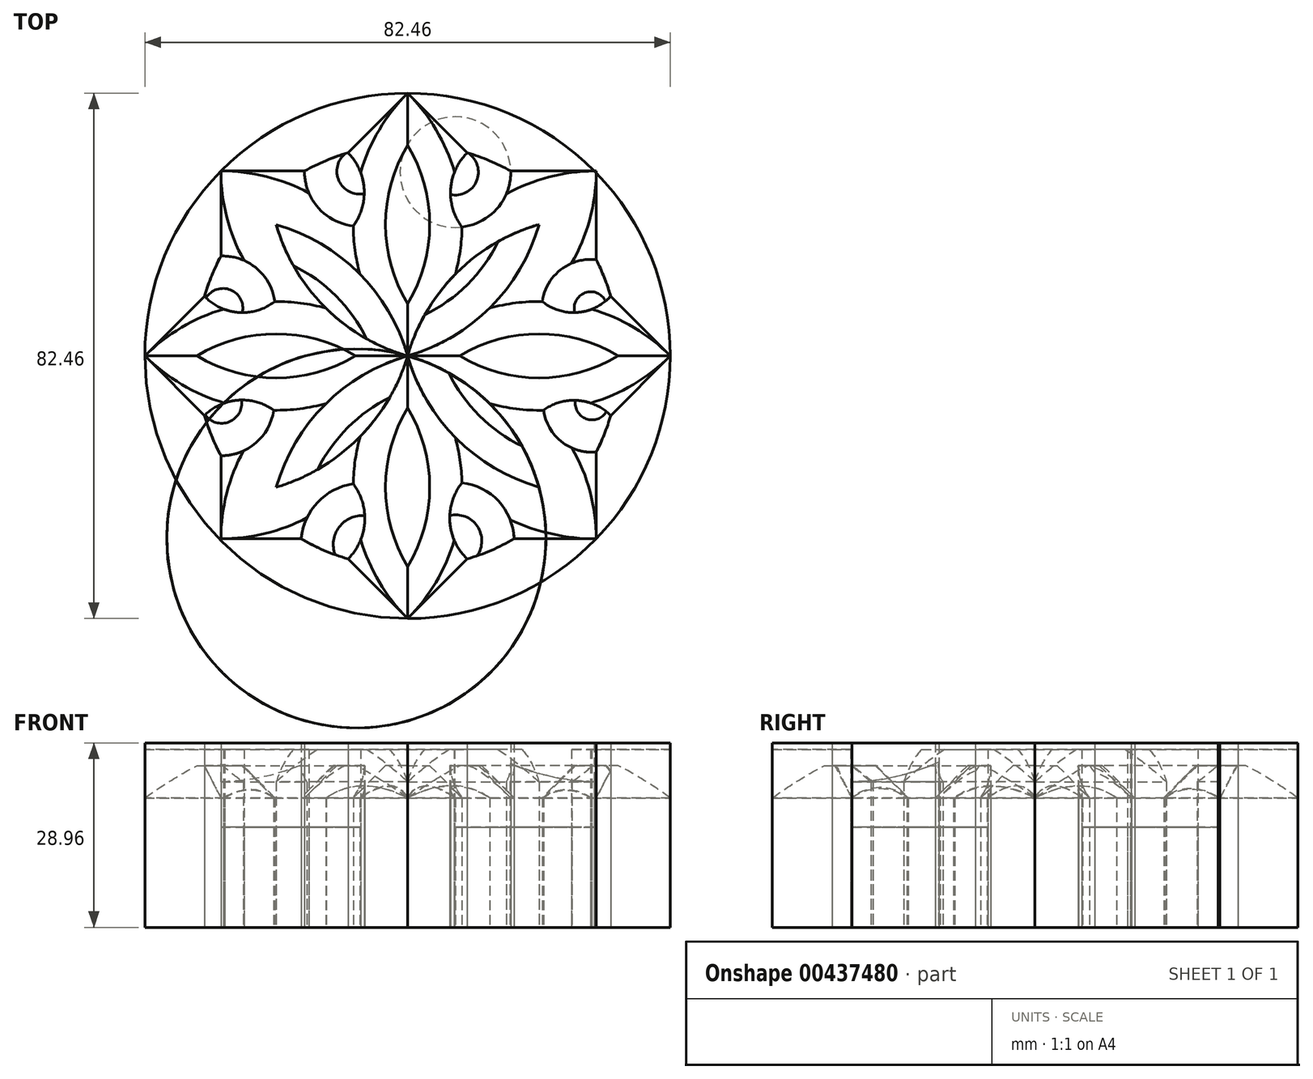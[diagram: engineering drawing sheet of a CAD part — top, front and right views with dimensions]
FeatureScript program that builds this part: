
annotation { "Feature Type Name" : "Feature", "Feature Type Description" : "" }
export const myFeature = defineFeature(function(context is Context, id is Id, definition is map)
    precondition{}
    {
        {
            var Q0;
            Q0=qCreatedBy(makeId("Top.planeOp"),FACE);
            var sketch = newSketch(context, id + "F0", { "sketchPlane" : qUnion([Q0])});
            skCircle(sketch, "E0", {"center": v(0, 0) * mm, "radius": 41.23 * mm});
            skArc(sketch, "E1", {"start": v(-9.36, 31.87) * mm, "mid": v(-12.85, 30.63) * mm, "end": v(-16.18, 29.01) * mm});
            skLineSegment(sketch, "E2", {"start": v(41.23, 0) * mm, "end": v(31.87, 9.36) * mm});
            skLineSegment(sketch, "E3", {"start": v(0, 41.23) * mm, "end": v(-9.36, 31.87) * mm});
            skLineSegment(sketch, "E4", {"start": v(-41.23, 0) * mm, "end": v(-31.87, -9.36) * mm});
            skLineSegment(sketch, "E5", {"start": v(0, -41.23) * mm, "end": v(9.36, -31.87) * mm});
            skLineSegment(sketch, "E6.bottom", {"start": v(-29.3, 29.01) * mm, "end": v(-16.18, 29.01) * mm});
            skLineSegment(sketch, "E6.top", {"start": v(-29.3, -28.71) * mm, "end": v(-16.71, -28.71) * mm});
            skLineSegment(sketch, "E6.left", {"start": v(-29.3, 29.01) * mm, "end": v(-29.3, 15.66) * mm});
            skLineSegment(sketch, "E6.right", {"start": v(29.6, 29.01) * mm, "end": v(29.6, 15.1) * mm});
            skLineSegment(sketch, "E7.trimOffspring", {"start": v(-31.87, 9.36) * mm, "end": v(-41.23, 0) * mm});
            skLineSegment(sketch, "E8.trimOffspring", {"start": v(-9.36, -31.87) * mm, "end": v(0, -41.23) * mm});
            skLineSegment(sketch, "E9.trimOffspring", {"start": v(31.87, -9.36) * mm, "end": v(41.23, 0) * mm});
            skLineSegment(sketch, "E10.trimOffspring", {"start": v(9.36, 31.87) * mm, "end": v(0, 41.23) * mm});
            skLineSegment(sketch, "E11.trimOffspring", {"start": v(16.18, 29.01) * mm, "end": v(29.6, 29.01) * mm});
            skLineSegment(sketch, "E12.trimOffspring", {"start": v(29.6, -15.1) * mm, "end": v(29.6, -28.71) * mm});
            skLineSegment(sketch, "E13.trimOffspring", {"start": v(-29.3, -15.66) * mm, "end": v(-29.3, -28.71) * mm});
            skLineSegment(sketch, "E14.trimOffspring", {"start": v(16.71, -28.71) * mm, "end": v(29.6, -28.71) * mm});
            skArc(sketch, "E15.trimOffspring", {"start": v(-29.3, 15.66) * mm, "mid": v(-30.75, 12.57) * mm, "end": v(-31.87, 9.36) * mm});
            skArc(sketch, "E16.trimOffspring", {"start": v(-31.87, -9.36) * mm, "mid": v(-30.75, -12.57) * mm, "end": v(-29.3, -15.66) * mm});
            skArc(sketch, "E17.trimOffspring", {"start": v(-16.71, -28.71) * mm, "mid": v(-13.13, -30.51) * mm, "end": v(-9.36, -31.87) * mm});
            skArc(sketch, "E18.trimOffspring", {"start": v(9.36, -31.87) * mm, "mid": v(13.13, -30.51) * mm, "end": v(16.71, -28.71) * mm});
            skArc(sketch, "E19.trimOffspring", {"start": v(29.6, -15.1) * mm, "mid": v(30.87, -12.28) * mm, "end": v(31.87, -9.36) * mm});
            skArc(sketch, "E20.trimOffspring", {"start": v(31.87, 9.36) * mm, "mid": v(30.87, 12.28) * mm, "end": v(29.6, 15.1) * mm});
            skArc(sketch, "E21.trimOffspring", {"start": v(16.18, 29.01) * mm, "mid": v(12.85, 30.63) * mm, "end": v(9.36, 31.87) * mm});
            skArc(sketch, "E22", {"start": v(7.47, 12.8) * mm, "mid": v(8.24, 16.47) * mm, "end": v(8.54, 20.21) * mm});
            skArc(sketch, "E23", {"start": v(0, 41.23) * mm, "mid": v(-4.47, 35.47) * mm, "end": v(-7.37, 28.78) * mm});
            skArc(sketch, "E24", {"start": v(29.6, 29.01) * mm, "mid": v(22.32, 28.1) * mm, "end": v(15.5, 25.44) * mm});
            skArc(sketch, "E25", {"start": v(41.23, 0) * mm, "mid": v(35.53, 4.43) * mm, "end": v(28.92, 7.33) * mm});
            skArc(sketch, "E26", {"start": v(12.9, -7.5) * mm, "mid": v(17.06, -8.32) * mm, "end": v(21.3, -8.53) * mm});
            skArc(sketch, "E27", {"start": v(29.6, -28.71) * mm, "mid": v(28.63, -21.34) * mm, "end": v(25.8, -14.46) * mm});
            skArc(sketch, "E28", {"start": v(0, -41.23) * mm, "mid": v(4.43, -35.54) * mm, "end": v(7.32, -28.94) * mm});
            skArc(sketch, "E29", {"start": v(-7.43, -12.63) * mm, "mid": v(-8.22, -16.32) * mm, "end": v(-8.53, -20.08) * mm});
            skArc(sketch, "E30", {"start": v(-29.3, -28.71) * mm, "mid": v(-22.35, -27.87) * mm, "end": v(-15.79, -25.41) * mm});
            skArc(sketch, "E31", {"start": v(-41.23, 0) * mm, "mid": v(-35.44, -4.49) * mm, "end": v(-28.72, -7.4) * mm});
            skArc(sketch, "E32", {"start": v(-12.82, 7.48) * mm, "mid": v(-16.8, 8.29) * mm, "end": v(-20.84, 8.54) * mm});
            skArc(sketch, "E33", {"start": v(-15.48, 25.55) * mm, "mid": v(-22.17, 28.13) * mm, "end": v(-29.3, 29.01) * mm});
            skArc(sketch, "E34", {"start": v(-29.3, 29.01) * mm, "mid": v(-28.38, 21.76) * mm, "end": v(-25.68, 14.98) * mm});
            skArc(sketch, "E35.trimOffspring", {"start": v(-25.77, -14.91) * mm, "mid": v(-28.4, -21.59) * mm, "end": v(-29.3, -28.71) * mm});
            skArc(sketch, "E36.trimOffspring", {"start": v(25.72, 14.52) * mm, "mid": v(28.6, 21.51) * mm, "end": v(29.6, 29.01) * mm});
            skArc(sketch, "E37", {"start": v(-8.54, 20.39) * mm, "mid": v(-6.83, 26.28) * mm, "end": v(-9.36, 31.87) * mm});
            skArc(sketch, "E38", {"start": v(-16.18, 29.01) * mm, "mid": v(-14.01, 23.24) * mm, "end": v(-8.54, 20.39) * mm});
            skArc(sketch, "E39", {"start": v(9.36, 31.87) * mm, "mid": v(6.76, 26.2) * mm, "end": v(8.54, 20.21) * mm});
            skArc(sketch, "E40", {"start": v(8.54, 20.21) * mm, "mid": v(14.06, 23.14) * mm, "end": v(16.18, 29.01) * mm});
            skArc(sketch, "E41", {"start": v(29.6, 15.1) * mm, "mid": v(24.03, 13.53) * mm, "end": v(21.13, 8.53) * mm});
            skArc(sketch, "E42", {"start": v(21.13, 8.53) * mm, "mid": v(26.67, 6.82) * mm, "end": v(31.87, 9.36) * mm});
            skArc(sketch, "E43", {"start": v(-20.84, 8.54) * mm, "mid": v(-23.69, 13.74) * mm, "end": v(-29.3, 15.66) * mm});
            skArc(sketch, "E44", {"start": v(-31.87, 9.36) * mm, "mid": v(-26.52, 6.81) * mm, "end": v(-20.84, 8.54) * mm});
            skArc(sketch, "E45", {"start": v(-21.02, -8.54) * mm, "mid": v(-26.6, -6.95) * mm, "end": v(-31.87, -9.36) * mm});
            skArc(sketch, "E46", {"start": v(-29.3, -15.66) * mm, "mid": v(-23.81, -13.66) * mm, "end": v(-21.02, -8.54) * mm});
            skArc(sketch, "E47", {"start": v(-8.53, -20.08) * mm, "mid": v(-14.11, -22.99) * mm, "end": v(-16.71, -28.71) * mm});
            skArc(sketch, "E48", {"start": v(-9.36, -31.87) * mm, "mid": v(-6.74, -26.13) * mm, "end": v(-8.53, -20.08) * mm});
            skArc(sketch, "E49", {"start": v(8.53, -19.91) * mm, "mid": v(6.63, -26.05) * mm, "end": v(9.36, -31.87) * mm});
            skArc(sketch, "E50", {"start": v(16.71, -28.71) * mm, "mid": v(14.26, -22.79) * mm, "end": v(8.53, -19.91) * mm});
            skArc(sketch, "E51", {"start": v(31.87, -9.36) * mm, "mid": v(26.74, -7) * mm, "end": v(21.3, -8.53) * mm});
            skArc(sketch, "E52", {"start": v(21.3, -8.53) * mm, "mid": v(24.15, -13.46) * mm, "end": v(29.6, -15.1) * mm});
            skArc(sketch, "E53.trimOffspring", {"start": v(-8.54, 20.39) * mm, "mid": v(-8.26, 16.57) * mm, "end": v(-7.48, 12.82) * mm});
            skArc(sketch, "E54.trimOffspring", {"start": v(-28.87, 7.35) * mm, "mid": v(-35.51, 4.45) * mm, "end": v(-41.23, 0) * mm});
            skArc(sketch, "E55.trimOffspring", {"start": v(-21.02, -8.54) * mm, "mid": v(-16.86, -8.3) * mm, "end": v(-12.79, -7.47) * mm});
            skArc(sketch, "E56.trimOffspring", {"start": v(-7.36, -28.83) * mm, "mid": v(-4.46, -35.5) * mm, "end": v(0, -41.23) * mm});
            skArc(sketch, "E57.trimOffspring", {"start": v(8.53, -19.91) * mm, "mid": v(8.22, -16.3) * mm, "end": v(7.46, -12.77) * mm});
            skArc(sketch, "E58.trimOffspring", {"start": v(28.7, -7.4) * mm, "mid": v(35.44, -4.5) * mm, "end": v(41.23, 0) * mm});
            skArc(sketch, "E59.trimOffspring", {"start": v(7.36, 28.84) * mm, "mid": v(4.46, 35.5) * mm, "end": v(0, 41.23) * mm});
            skArc(sketch, "E60.trimOffspring", {"start": v(21.13, 8.53) * mm, "mid": v(16.96, 8.3) * mm, "end": v(12.86, 7.49) * mm});
            skArc(sketch, "E61", {"start": v(0, 0) * mm, "mid": v(-7.64, 12.98) * mm, "end": v(-20.62, 20.62) * mm});
            skArc(sketch, "E62", {"start": v(-20.62, 20.62) * mm, "mid": v(-12.98, 7.63) * mm, "end": v(0, 0) * mm});
            skArc(sketch, "E63", {"start": v(20.62, 20.62) * mm, "mid": v(7.64, 12.97) * mm, "end": v(0, 0) * mm});
            skArc(sketch, "E64", {"start": v(0, 0) * mm, "mid": v(13, 7.62) * mm, "end": v(20.62, 20.62) * mm});
            skArc(sketch, "E65", {"start": v(20.62, -20.62) * mm, "mid": v(13, -7.61) * mm, "end": v(0, 0) * mm});
            skArc(sketch, "E66", {"start": v(0, 0) * mm, "mid": v(7.65, -12.96) * mm, "end": v(20.62, -20.62) * mm});
            skArc(sketch, "E67", {"start": v(-20.62, -20.62) * mm, "mid": v(-7.7, -12.91) * mm, "end": v(0, 0) * mm});
            skArc(sketch, "E68", {"start": v(0, 0) * mm, "mid": v(-12.97, -7.65) * mm, "end": v(-20.62, -20.62) * mm});
            skArc(sketch, "E69", {"start": v(16.1, -25.72) * mm, "mid": v(22.68, -27.95) * mm, "end": v(29.6, -28.71) * mm});
            skSolve(sketch);
        }
        {
            var Q0;
            {var subQ0=sQuery(id+"F0.wireOp",EDGE,"E6.right");var subQ1=sQuery(id+"F0.wireOp",EDGE,"E0");var subQ2=makeQuery(id+"F0.imprint","INTERSECT",VERTEX,{"derivedFrom":[subQ1,subQ0]});Q0=makeQuery(id+"F0.imprint","IMPRINT",FACE,{"disambiguationData":[TD([[makeQuery(id+"F0.imprint","IMPRINT",EDGE,{"disambiguationData":[TD([[subQ2,-1.0]])],"derivedFrom":subQ1}),-1.0]])]});}
            var Q1;
            {var subQ0=sQuery(id+"F0.wireOp",EDGE,"E11.trimOffspring");var subQ1=sQuery(id+"F0.wireOp",EDGE,"E0");var subQ2=makeQuery(id+"F0.imprint","INTERSECT",VERTEX,{"derivedFrom":[subQ1,subQ0]});Q1=makeQuery(id+"F0.imprint","IMPRINT",FACE,{"disambiguationData":[TD([[makeQuery(id+"F0.imprint","IMPRINT",EDGE,{"disambiguationData":[TD([[subQ2,1.0]])],"derivedFrom":subQ1}),-1.0]])]});}
            var Q2;
            {var subQ0=sQuery(id+"F0.wireOp",EDGE,"E2");Q2=makeQuery(id+"F0.imprint","IMPRINT",FACE,{"disambiguationData":[TD([[makeQuery(id+"F0.imprint","IMPRINT",EDGE,{"derivedFrom":subQ0}),-1.0]])]});}
            var Q3;
            {var subQ0=sQuery(id+"F0.wireOp",EDGE,"E36.trimOffspring");var subQ1=sQuery(id+"F0.wireOp",EDGE,"E0");var subQ2=makeQuery(id+"F0.imprint","INTERSECT",VERTEX,{"derivedFrom":[subQ1,subQ0]});Q3=makeQuery(id+"F0.imprint","IMPRINT",FACE,{"disambiguationData":[TD([[makeQuery(id+"F0.imprint","IMPRINT",EDGE,{"disambiguationData":[TD([[subQ2,-1.0]])],"derivedFrom":subQ1}),-1.0]])]});}
            var Q4;
            {var subQ0=sQuery(id+"F0.wireOp",EDGE,"E10.trimOffspring");Q4=makeQuery(id+"F0.imprint","IMPRINT",FACE,{"disambiguationData":[TD([[makeQuery(id+"F0.imprint","IMPRINT",EDGE,{"derivedFrom":subQ0}),-1.0]])]});}
            var Q5;
            Q5=makeQuery(id+"F0.imprint","IMPRINT",FACE,{"disambiguationData":[TD([[makeQuery(id+"F0.imprint","IMPRINT",EDGE,{"derivedFrom":sQuery(id+"F0.wireOp",EDGE,"E1")}),-1.0]])]});
            var Q6;
            {var subQ2=sQuery(id+"F0.wireOp",EDGE,"E6.left");Q6=makeQuery(id+"F0.imprint","IMPRINT",FACE,{"disambiguationData":[TD([[makeQuery(id+"F0.imprint","IMPRINT",EDGE,{"derivedFrom":subQ2}),-1.0]])]});}
            var Q7;
            {var subQ0=sQuery(id+"F0.wireOp",EDGE,"E5");Q7=makeQuery(id+"F0.imprint","IMPRINT",FACE,{"disambiguationData":[TD([[makeQuery(id+"F0.imprint","IMPRINT",EDGE,{"derivedFrom":subQ0}),-1.0]])]});}
            var Q8;
            {var subQ0=sQuery(id+"F0.wireOp",EDGE,"E9.trimOffspring");Q8=makeQuery(id+"F0.imprint","IMPRINT",FACE,{"disambiguationData":[TD([[makeQuery(id+"F0.imprint","IMPRINT",EDGE,{"derivedFrom":subQ0}),-1.0]])]});}
            var Q9;
            {var subQ1=sQuery(id+"F0.wireOp",EDGE,"E4");Q9=makeQuery(id+"F0.imprint","IMPRINT",FACE,{"disambiguationData":[TD([[makeQuery(id+"F0.imprint","IMPRINT",EDGE,{"derivedFrom":subQ1}),-1.0]])]});}
            extrude(context, id + "F1", {"entities" : qUnion([Q0, Q1, Q2, Q3, Q4, Q5, Q6, Q7, Q8, Q9]), "depth" : 28.96 * mm});
        }
        {
            var Q0;
            {var subQ4=sQuery(id+"F0.wireOp",EDGE,"E32");Q0=makeQuery(id+"F0.imprint","IMPRINT",FACE,{"disambiguationData":[TD([[makeQuery(id+"F0.imprint","IMPRINT",EDGE,{"derivedFrom":subQ4}),-1.0]])]});}
            var Q1;
            {var subQ10=sQuery(id+"F0.wireOp",EDGE,"E22");Q1=makeQuery(id+"F0.imprint","IMPRINT",FACE,{"disambiguationData":[TD([[makeQuery(id+"F0.imprint","IMPRINT",EDGE,{"derivedFrom":subQ10}),-1.0]])]});}
            var Q2;
            {var subQ1=sQuery(id+"F0.wireOp",EDGE,"E26");Q2=makeQuery(id+"F0.imprint","IMPRINT",FACE,{"disambiguationData":[TD([[makeQuery(id+"F0.imprint","IMPRINT",EDGE,{"derivedFrom":subQ1}),-1.0]])]});}
            var Q3;
            {var subQ4=sQuery(id+"F0.wireOp",EDGE,"E29");Q3=makeQuery(id+"F0.imprint","IMPRINT",FACE,{"disambiguationData":[TD([[makeQuery(id+"F0.imprint","IMPRINT",EDGE,{"derivedFrom":subQ4}),-1.0]])]});}
            extrude(context, id + "F2", {"entities" : qUnion([Q0, Q1, Q2, Q3]), "operationType" : NewBodyOperationType.ADD, "depth" : 15.75 * mm});
        }
        {
            var Q0;
            {var subQ1=sQuery(id+"F0.wireOp",EDGE,"E31");Q0=makeQuery(id+"F0.imprint","IMPRINT",FACE,{"disambiguationData":[TD([[makeQuery(id+"F0.imprint","IMPRINT",EDGE,{"derivedFrom":subQ1}),1.0]])]});}
            var Q1;
            {var subQ4=sQuery(id+"F0.wireOp",EDGE,"E25");Q1=makeQuery(id+"F0.imprint","IMPRINT",FACE,{"disambiguationData":[TD([[makeQuery(id+"F0.imprint","IMPRINT",EDGE,{"derivedFrom":subQ4}),1.0]])]});}
            var Q2;
            {var subQ1=sQuery(id+"F0.wireOp",EDGE,"E28");Q2=makeQuery(id+"F0.imprint","IMPRINT",FACE,{"disambiguationData":[TD([[makeQuery(id+"F0.imprint","IMPRINT",EDGE,{"derivedFrom":subQ1}),1.0]])]});}
            var Q3;
            {var subQ1=sQuery(id+"F0.wireOp",EDGE,"E22");Q3=makeQuery(id+"F0.imprint","IMPRINT",FACE,{"disambiguationData":[TD([[makeQuery(id+"F0.imprint","IMPRINT",EDGE,{"derivedFrom":subQ1}),1.0]])]});}
            extrude(context, id + "F3", {"entities" : qUnion([Q0, Q1, Q2, Q3]), "depth" : 25.4 * mm});
        }
        {
            var Q0;
            {var subQ0=sQuery(id+"F0.wireOp",EDGE,"E6.bottom");Q0=makeQuery(id+"F0.imprint","IMPRINT",FACE,{"disambiguationData":[TD([[makeQuery(id+"F0.imprint","IMPRINT",EDGE,{"derivedFrom":subQ0}),-1.0]])]});}
            var Q1;
            {var subQ0=sQuery(id+"F0.wireOp",EDGE,"E6.left");Q1=makeQuery(id+"F0.imprint","IMPRINT",FACE,{"disambiguationData":[TD([[makeQuery(id+"F0.imprint","IMPRINT",EDGE,{"derivedFrom":subQ0}),1.0]])]});}
            var Q2;
            {var subQ0=sQuery(id+"F0.wireOp",EDGE,"E7.trimOffspring");Q2=makeQuery(id+"F0.imprint","IMPRINT",FACE,{"disambiguationData":[TD([[makeQuery(id+"F0.imprint","IMPRINT",EDGE,{"derivedFrom":subQ0}),1.0]])]});}
            var Q3;
            {var subQ0=sQuery(id+"F0.wireOp",EDGE,"E4");Q3=makeQuery(id+"F0.imprint","IMPRINT",FACE,{"disambiguationData":[TD([[makeQuery(id+"F0.imprint","IMPRINT",EDGE,{"derivedFrom":subQ0}),1.0]])]});}
            var Q4;
            {var subQ0=sQuery(id+"F0.wireOp",EDGE,"E13.trimOffspring");Q4=makeQuery(id+"F0.imprint","IMPRINT",FACE,{"disambiguationData":[TD([[makeQuery(id+"F0.imprint","IMPRINT",EDGE,{"derivedFrom":subQ0}),1.0]])]});}
            var Q5;
            {var subQ0=sQuery(id+"F0.wireOp",EDGE,"E6.top");Q5=makeQuery(id+"F0.imprint","IMPRINT",FACE,{"disambiguationData":[TD([[makeQuery(id+"F0.imprint","IMPRINT",EDGE,{"derivedFrom":subQ0}),1.0]])]});}
            var Q6;
            {var subQ0=sQuery(id+"F0.wireOp",EDGE,"E8.trimOffspring");Q6=makeQuery(id+"F0.imprint","IMPRINT",FACE,{"disambiguationData":[TD([[makeQuery(id+"F0.imprint","IMPRINT",EDGE,{"derivedFrom":subQ0}),1.0]])]});}
            var Q7;
            {var subQ0=sQuery(id+"F0.wireOp",EDGE,"E5");Q7=makeQuery(id+"F0.imprint","IMPRINT",FACE,{"disambiguationData":[TD([[makeQuery(id+"F0.imprint","IMPRINT",EDGE,{"derivedFrom":subQ0}),1.0]])]});}
            var Q8;
            {var subQ0=sQuery(id+"F0.wireOp",EDGE,"E14.trimOffspring");Q8=makeQuery(id+"F0.imprint","IMPRINT",FACE,{"disambiguationData":[TD([[makeQuery(id+"F0.imprint","IMPRINT",EDGE,{"derivedFrom":subQ0}),1.0]])]});}
            var Q9;
            {var subQ0=sQuery(id+"F0.wireOp",EDGE,"E12.trimOffspring");Q9=makeQuery(id+"F0.imprint","IMPRINT",FACE,{"disambiguationData":[TD([[makeQuery(id+"F0.imprint","IMPRINT",EDGE,{"derivedFrom":subQ0}),-1.0]])]});}
            var Q10;
            {var subQ0=sQuery(id+"F0.wireOp",EDGE,"E9.trimOffspring");Q10=makeQuery(id+"F0.imprint","IMPRINT",FACE,{"disambiguationData":[TD([[makeQuery(id+"F0.imprint","IMPRINT",EDGE,{"derivedFrom":subQ0}),1.0]])]});}
            var Q11;
            {var subQ0=sQuery(id+"F0.wireOp",EDGE,"E2");Q11=makeQuery(id+"F0.imprint","IMPRINT",FACE,{"disambiguationData":[TD([[makeQuery(id+"F0.imprint","IMPRINT",EDGE,{"derivedFrom":subQ0}),1.0]])]});}
            var Q12;
            {var subQ0=sQuery(id+"F0.wireOp",EDGE,"E6.right");var subQ1=sQuery(id+"F0.wireOp",EDGE,"E0");var subQ2=makeQuery(id+"F0.imprint","INTERSECT",VERTEX,{"derivedFrom":[subQ1,subQ0]});Q12=makeQuery(id+"F0.imprint","IMPRINT",FACE,{"disambiguationData":[TD([[makeQuery(id+"F0.imprint","IMPRINT",EDGE,{"disambiguationData":[TD([[subQ2,-1.0]])],"derivedFrom":subQ1}),1.0]])]});}
            var Q13;
            {var subQ0=sQuery(id+"F0.wireOp",EDGE,"E11.trimOffspring");var subQ1=sQuery(id+"F0.wireOp",EDGE,"E0");var subQ2=makeQuery(id+"F0.imprint","INTERSECT",VERTEX,{"derivedFrom":[subQ1,subQ0]});Q13=makeQuery(id+"F0.imprint","IMPRINT",FACE,{"disambiguationData":[TD([[makeQuery(id+"F0.imprint","IMPRINT",EDGE,{"disambiguationData":[TD([[subQ2,1.0]])],"derivedFrom":subQ1}),1.0]])]});}
            var Q14;
            {var subQ0=sQuery(id+"F0.wireOp",EDGE,"E10.trimOffspring");Q14=makeQuery(id+"F0.imprint","IMPRINT",FACE,{"disambiguationData":[TD([[makeQuery(id+"F0.imprint","IMPRINT",EDGE,{"derivedFrom":subQ0}),1.0]])]});}
            var Q15;
            {var subQ0=sQuery(id+"F0.wireOp",EDGE,"E3");Q15=makeQuery(id+"F0.imprint","IMPRINT",FACE,{"disambiguationData":[TD([[makeQuery(id+"F0.imprint","IMPRINT",EDGE,{"derivedFrom":subQ0}),1.0]])]});}
            var Q16;
            {var subQ0=sQuery(id+"F0.wireOp",EDGE,"E61");var subQ1=makeQuery(id+"F0.imprint","INTERSECT",VERTEX,{"derivedFrom":[sQuery(id+"F0.wireOp",EDGE,"E53.trimOffspring"),subQ0]});Q16=makeQuery(id+"F0.imprint","IMPRINT",FACE,{"disambiguationData":[TD([[makeQuery(id+"F0.imprint","IMPRINT",EDGE,{"disambiguationData":[TD([[subQ1,-1.0]])],"derivedFrom":subQ0}),1.0]])]});}
            var Q17;
            {var subQ0=sQuery(id+"F0.wireOp",EDGE,"E67");var subQ1=makeQuery(id+"F0.imprint","INTERSECT",VERTEX,{"derivedFrom":[sQuery(id+"F0.wireOp",EDGE,"E29"),subQ0]});Q17=makeQuery(id+"F0.imprint","IMPRINT",FACE,{"disambiguationData":[TD([[makeQuery(id+"F0.imprint","IMPRINT",EDGE,{"disambiguationData":[TD([[subQ1,1.0]])],"derivedFrom":subQ0}),1.0]])]});}
            var Q18;
            {var subQ0=sQuery(id+"F0.wireOp",EDGE,"E65");var subQ1=makeQuery(id+"F0.imprint","INTERSECT",VERTEX,{"derivedFrom":[sQuery(id+"F0.wireOp",EDGE,"E26"),subQ0]});Q18=makeQuery(id+"F0.imprint","IMPRINT",FACE,{"disambiguationData":[TD([[makeQuery(id+"F0.imprint","IMPRINT",EDGE,{"disambiguationData":[TD([[subQ1,1.0]])],"derivedFrom":subQ0}),1.0]])]});}
            var Q19;
            {var subQ0=sQuery(id+"F0.wireOp",EDGE,"E63");var subQ1=makeQuery(id+"F0.imprint","INTERSECT",VERTEX,{"derivedFrom":[sQuery(id+"F0.wireOp",EDGE,"E22"),subQ0]});Q19=makeQuery(id+"F0.imprint","IMPRINT",FACE,{"disambiguationData":[TD([[makeQuery(id+"F0.imprint","IMPRINT",EDGE,{"disambiguationData":[TD([[subQ1,1.0]])],"derivedFrom":subQ0}),1.0]])]});}
            extrude(context, id + "F4", {"entities" : qUnion([Q0, Q1, Q2, Q3, Q4, Q5, Q6, Q7, Q8, Q9, Q10, Q11, Q12, Q13, Q14, Q15, Q16, Q17, Q18, Q19]), "depth" : 27.94 * mm});
        }
        {
            var Q0;
            {var subQ1=sQuery(id+"F0.wireOp",EDGE,"E1");Q0=makeQuery(id+"F0.imprint","IMPRINT",FACE,{"disambiguationData":[TD([[makeQuery(id+"F0.imprint","IMPRINT",EDGE,{"derivedFrom":subQ1}),1.0]])]});}
            var Q1;
            {var subQ1=sQuery(id+"F0.wireOp",EDGE,"E15.trimOffspring");Q1=makeQuery(id+"F0.imprint","IMPRINT",FACE,{"disambiguationData":[TD([[makeQuery(id+"F0.imprint","IMPRINT",EDGE,{"derivedFrom":subQ1}),1.0]])]});}
            var Q2;
            {var subQ1=sQuery(id+"F0.wireOp",EDGE,"E16.trimOffspring");Q2=makeQuery(id+"F0.imprint","IMPRINT",FACE,{"disambiguationData":[TD([[makeQuery(id+"F0.imprint","IMPRINT",EDGE,{"derivedFrom":subQ1}),1.0]])]});}
            var Q3;
            {var subQ1=sQuery(id+"F0.wireOp",EDGE,"E17.trimOffspring");Q3=makeQuery(id+"F0.imprint","IMPRINT",FACE,{"disambiguationData":[TD([[makeQuery(id+"F0.imprint","IMPRINT",EDGE,{"derivedFrom":subQ1}),1.0]])]});}
            var Q4;
            {var subQ1=sQuery(id+"F0.wireOp",EDGE,"E18.trimOffspring");Q4=makeQuery(id+"F0.imprint","IMPRINT",FACE,{"disambiguationData":[TD([[makeQuery(id+"F0.imprint","IMPRINT",EDGE,{"derivedFrom":subQ1}),1.0]])]});}
            var Q5;
            {var subQ4=sQuery(id+"F0.wireOp",EDGE,"E19.trimOffspring");Q5=makeQuery(id+"F0.imprint","IMPRINT",FACE,{"disambiguationData":[TD([[makeQuery(id+"F0.imprint","IMPRINT",EDGE,{"derivedFrom":subQ4}),1.0]])]});}
            var Q6;
            {var subQ5=sQuery(id+"F0.wireOp",EDGE,"E20.trimOffspring");Q6=makeQuery(id+"F0.imprint","IMPRINT",FACE,{"disambiguationData":[TD([[makeQuery(id+"F0.imprint","IMPRINT",EDGE,{"derivedFrom":subQ5}),1.0]])]});}
            var Q7;
            {var subQ5=sQuery(id+"F0.wireOp",EDGE,"E21.trimOffspring");Q7=makeQuery(id+"F0.imprint","IMPRINT",FACE,{"disambiguationData":[TD([[makeQuery(id+"F0.imprint","IMPRINT",EDGE,{"derivedFrom":subQ5}),1.0]])]});}
            extrude(context, id + "F5", {"entities" : qUnion([Q0, Q1, Q2, Q3, Q4, Q5, Q6, Q7]), "depth" : 25.4 * mm});
        }
        {
            var Q0;
            Q0=makeQuery(id+"F4.opExtrude","CAP_EDGE",EDGE,{"disambiguationData":[OSD([sQuery(id+"F0.wireOp",EDGE,"E61")])],"isStart":false});
            var Q1;
            Q1=makeQuery(id+"F4.opExtrude","CAP_EDGE",EDGE,{"disambiguationData":[OSD([sQuery(id+"F0.wireOp",EDGE,"E68")])],"isStart":false});
            var Q2;
            Q2=makeQuery(id+"F4.opExtrude","CAP_EDGE",EDGE,{"disambiguationData":[OSD([sQuery(id+"F0.wireOp",EDGE,"E66")])],"isStart":false});
            var Q3;
            Q3=makeQuery(id+"F4.opExtrude","CAP_EDGE",EDGE,{"disambiguationData":[OSD([sQuery(id+"F0.wireOp",EDGE,"E64")])],"isStart":false});
            var Q4;
            Q4=makeQuery(id+"F3.opExtrude","CAP_EDGE",EDGE,{"disambiguationData":[OSD([sQuery(id+"F0.wireOp",EDGE,"E53.trimOffspring")])],"isStart":false});
            var Q5;
            Q5=makeQuery(id+"F3.opExtrude","CAP_EDGE",EDGE,{"disambiguationData":[OSD([sQuery(id+"F0.wireOp",EDGE,"E55.trimOffspring")])],"isStart":false});
            var Q6;
            Q6=makeQuery(id+"F3.opExtrude","CAP_EDGE",EDGE,{"disambiguationData":[OSD([sQuery(id+"F0.wireOp",EDGE,"E57.trimOffspring")])],"isStart":false});
            var Q7;
            Q7=makeQuery(id+"F3.opExtrude","CAP_EDGE",EDGE,{"disambiguationData":[OSD([sQuery(id+"F0.wireOp",EDGE,"E60.trimOffspring")])],"isStart":false});
            var Q8;
            Q8=makeQuery(id+"F3.opExtrude","CAP_EDGE",EDGE,{"disambiguationData":[OSD([sQuery(id+"F0.wireOp",EDGE,"E26")])],"isStart":false});
            var Q9;
            Q9=makeQuery(id+"F3.opExtrude","CAP_EDGE",EDGE,{"disambiguationData":[OSD([sQuery(id+"F0.wireOp",EDGE,"E29")])],"isStart":false});
            var Q10;
            Q10=makeQuery(id+"F3.opExtrude","CAP_EDGE",EDGE,{"disambiguationData":[OSD([sQuery(id+"F0.wireOp",EDGE,"E32")])],"isStart":false});
            var Q11;
            Q11=makeQuery(id+"F3.opExtrude","CAP_EDGE",EDGE,{"disambiguationData":[OSD([sQuery(id+"F0.wireOp",EDGE,"E22")])],"isStart":false});
            var Q12;
            Q12=makeQuery(id+"F5.opExtrude","CAP_EDGE",EDGE,{"disambiguationData":[OSD([sQuery(id+"F0.wireOp",EDGE,"E43")])],"isStart":false});
            var Q13;
            Q13=makeQuery(id+"F5.opExtrude","CAP_EDGE",EDGE,{"disambiguationData":[OSD([sQuery(id+"F0.wireOp",EDGE,"E38")])],"isStart":false});
            var Q14;
            Q14=makeQuery(id+"F5.opExtrude","CAP_EDGE",EDGE,{"disambiguationData":[OSD([sQuery(id+"F0.wireOp",EDGE,"E40")])],"isStart":false});
            var Q15;
            Q15=makeQuery(id+"F5.opExtrude","CAP_EDGE",EDGE,{"disambiguationData":[OSD([sQuery(id+"F0.wireOp",EDGE,"E41")])],"isStart":false});
            var Q16;
            Q16=makeQuery(id+"F5.opExtrude","CAP_EDGE",EDGE,{"disambiguationData":[OSD([sQuery(id+"F0.wireOp",EDGE,"E52")])],"isStart":false});
            var Q17;
            Q17=makeQuery(id+"F5.opExtrude","CAP_EDGE",EDGE,{"disambiguationData":[OSD([sQuery(id+"F0.wireOp",EDGE,"E50")])],"isStart":false});
            var Q18;
            Q18=makeQuery(id+"F5.opExtrude","CAP_EDGE",EDGE,{"disambiguationData":[OSD([sQuery(id+"F0.wireOp",EDGE,"E47")])],"isStart":false});
            var Q19;
            Q19=makeQuery(id+"F5.opExtrude","CAP_EDGE",EDGE,{"disambiguationData":[OSD([sQuery(id+"F0.wireOp",EDGE,"E46")])],"isStart":false});
            var Q20;
            Q20=makeQuery(id+"F4.opExtrude","CAP_EDGE",EDGE,{"disambiguationData":[OSD([sQuery(id+"F0.wireOp",EDGE,"E35.trimOffspring")])],"isStart":false});
            var Q21;
            Q21=makeQuery(id+"F4.opExtrude","CAP_EDGE",EDGE,{"disambiguationData":[OSD([sQuery(id+"F0.wireOp",EDGE,"E30")])],"isStart":false});
            var Q22;
            Q22=makeQuery(id+"F4.opExtrude","CAP_EDGE",EDGE,{"disambiguationData":[OSD([sQuery(id+"F0.wireOp",EDGE,"E27")])],"isStart":false});
            var Q23;
            Q23=makeQuery(id+"F4.opExtrude","CAP_EDGE",EDGE,{"disambiguationData":[OSD([sQuery(id+"F0.wireOp",EDGE,"E69")])],"isStart":false});
            var Q24;
            Q24=makeQuery(id+"F4.opExtrude","CAP_EDGE",EDGE,{"disambiguationData":[OSD([sQuery(id+"F0.wireOp",EDGE,"E24")])],"isStart":false});
            chamfer(context, id + "F6", {"entities" : qUnion([Q0, Q1, Q2, Q3, Q4, Q5, Q6, Q7, Q8, Q9, Q10, Q11, Q12, Q13, Q14, Q15, Q16, Q17, Q18, Q19, Q20, Q21, Q22, Q23, Q24]), "width" : 5.08 * mm, "tangentPropagation" : true});
        }
    });
